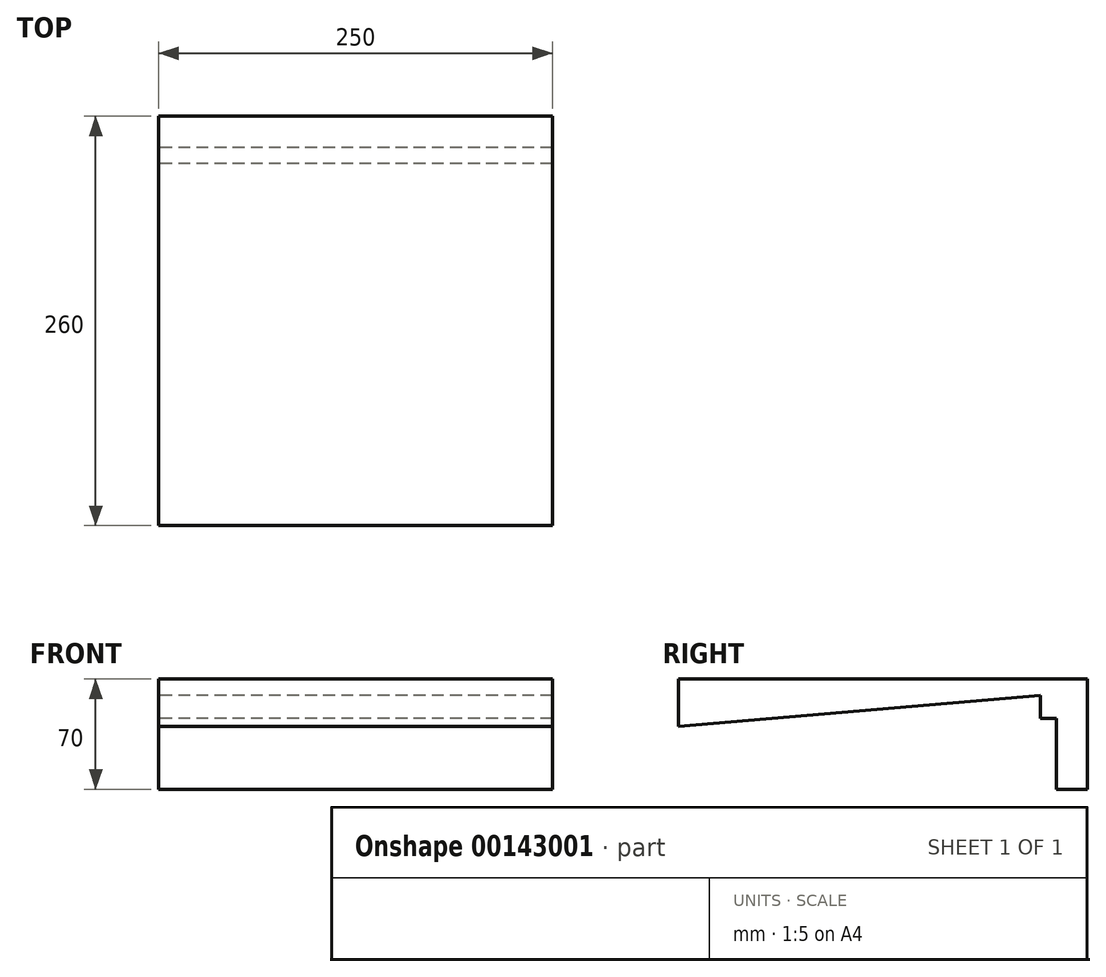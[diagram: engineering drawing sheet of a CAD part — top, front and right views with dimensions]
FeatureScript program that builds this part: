
annotation { "Feature Type Name" : "Feature", "Feature Type Description" : "" }
export const myFeature = defineFeature(function(context is Context, id is Id, definition is map)
    precondition{}
    {
        {
            var Q0;
            Q0=qCreatedBy(makeId("Right.planeOp"),FACE);
            var sketch = newSketch(context, id + "F0", { "sketchPlane" : qUnion([Q0])});
            skLineSegment(sketch, "E0", {"start": v(0, 0) * mm, "end": v(260, 0) * mm});
            skLineSegment(sketch, "E1", {"start": v(0, 0) * mm, "end": v(0, -30) * mm, "construction": true});
            skLineSegment(sketch, "E2", {"start": v(0, 0) * mm, "end": v(0, -30) * mm});
            skPoint(sketch, "E3", {"position": v(230, -10.35) * mm});
            skPoint(sketch, "E4", {"position": v(230, -25) * mm});
            skPoint(sketch, "E5", {"position": v(240, -25) * mm});
            skPoint(sketch, "E6", {"position": v(240, -70) * mm});
            skPoint(sketch, "E7", {"position": v(260, -70) * mm});
            skPoint(sketch, "E8", {"position": v(260, 0) * mm});
            skLineSegment(sketch, "E9", {"start": v(260, 0) * mm, "end": v(260, 0) * mm});
            skLineSegment(sketch, "E10", {"start": v(260, -70) * mm, "end": v(240, -70) * mm});
            skLineSegment(sketch, "E11", {"start": v(240, -25) * mm, "end": v(240, -70) * mm});
            skLineSegment(sketch, "E12", {"start": v(260, 0) * mm, "end": v(260, -70) * mm});
            skLineSegment(sketch, "E13", {"start": v(240, -25) * mm, "end": v(230, -25) * mm});
            skLineSegment(sketch, "E14", {"start": v(230, -25) * mm, "end": v(230, -10.35) * mm});
            skLineSegment(sketch, "E15", {"start": v(0, -30) * mm, "end": v(230, -10.35) * mm});
            skSolve(sketch);
        }
        {
            var Q0;
            Q0 = qSketchRegion(id + "F0", true);
            extrude(context, id + "F1", {"entities" : qUnion([Q0]), "depth" : 250 * mm, "offsetDistance" : 25 * mm});
        }
    });
